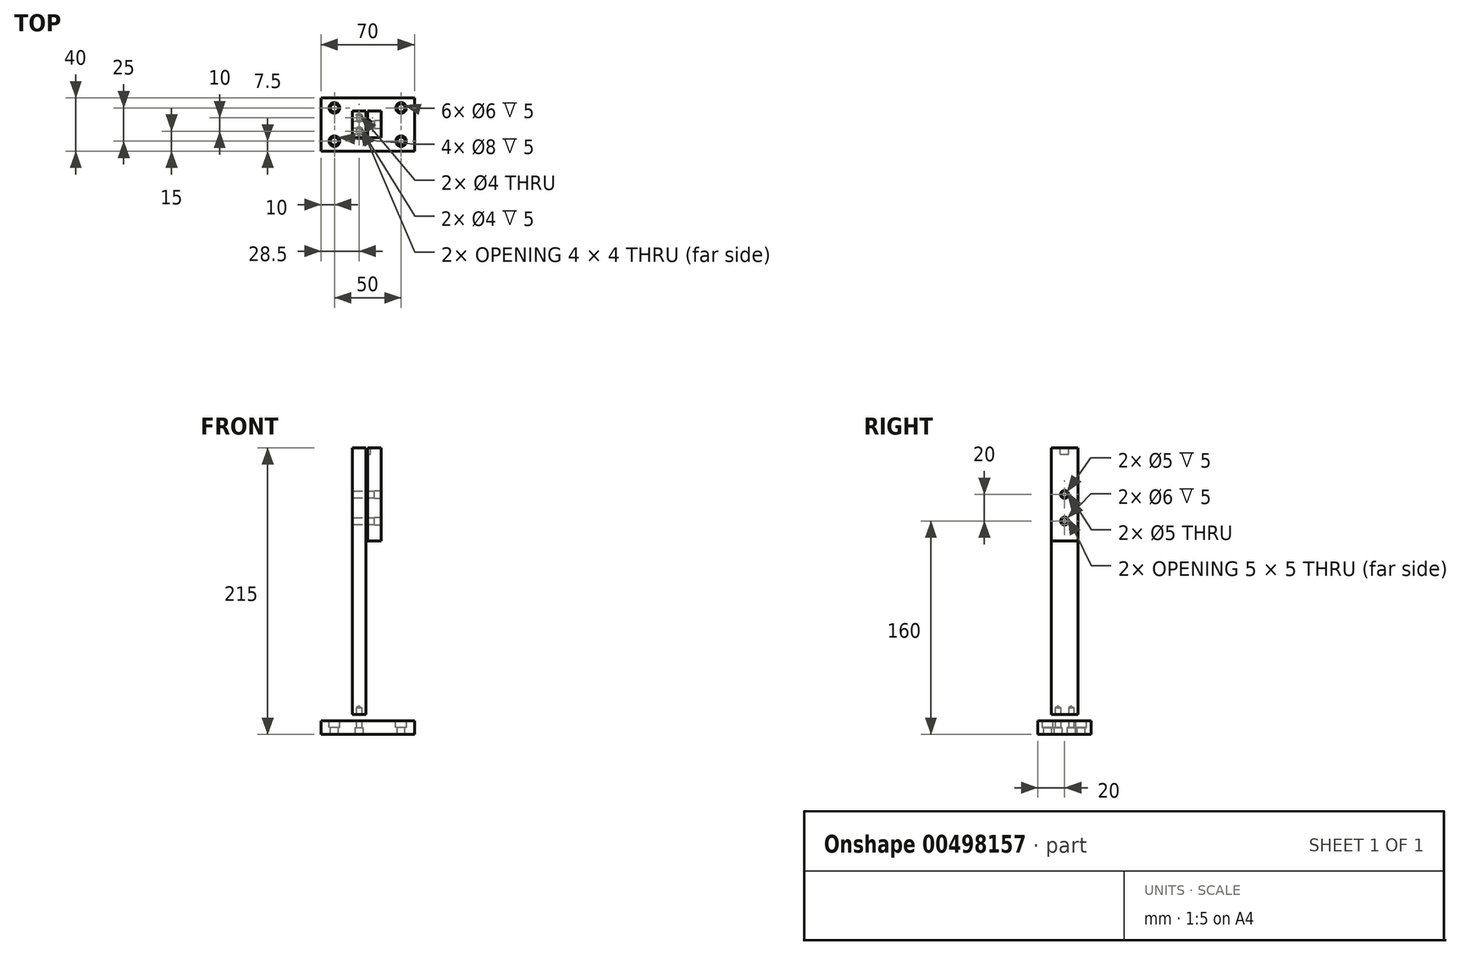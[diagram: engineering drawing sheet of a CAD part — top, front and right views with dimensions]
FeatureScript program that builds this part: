
annotation { "Feature Type Name" : "Feature", "Feature Type Description" : "" }
export const myFeature = defineFeature(function(context is Context, id is Id, definition is map)
    precondition{}
    {
        {
            var Q0;
            Q0=qCreatedBy(makeId("Top.planeOp"),FACE);
            var sketch = newSketch(context, id + "F0", { "sketchPlane" : qUnion([Q0])});
            skLineSegment(sketch, "E0.bottom", {"start": v(-35, 20) * mm, "end": v(35, 20) * mm});
            skLineSegment(sketch, "E0.top", {"start": v(-35, -20) * mm, "end": v(35, -20) * mm});
            skLineSegment(sketch, "E0.left", {"start": v(-35, 20) * mm, "end": v(-35, -20) * mm});
            skLineSegment(sketch, "E0.right", {"start": v(35, 20) * mm, "end": v(35, -20) * mm});
            skPoint(sketch, "E0.middle", {"position": v(0, 0) * mm});
            skSolve(sketch);
        }
        {
            var Q0;
            Q0=makeQuery(id+"F0.imprint","IMPRINT",FACE,{"disambiguationData":[TD([[makeQuery(id+"F0.imprint","IMPRINT",EDGE,{"derivedFrom":sQuery(id+"F0.wireOp",EDGE,"E0.bottom")}),-1.0]])]});
            extrude(context, id + "F1", {"entities" : qUnion([Q0]), "depth" : 10 * mm});
        }
        {
            var Q0;
            Q0=makeQuery(id+"F1.opExtrude","CAP_FACE",FACE,{"disambiguationData":[OSD([sQuery(id+"F0.wireOp",EDGE,"E0.bottom"),sQuery(id+"F0.wireOp",EDGE,"E0.top"),sQuery(id+"F0.wireOp",EDGE,"E0.left"),sQuery(id+"F0.wireOp",EDGE,"E0.right")])],"isStart":false});
            cPlane(context, id + "F2", {"entities" : qUnion([Q0]), "cplaneType" : CPlaneType.OFFSET, "offset" : 0 * mm, "width" : 150 * mm, "height" : 150 * mm});
        }
        {
            var Q0;
            Q0=qCreatedBy(id+"F2.planeOp",FACE);
            var sketch = newSketch(context, id + "F3", { "sketchPlane" : qUnion([Q0])});
            skLineSegment(sketch, "E1.bottom", {"start": v(25, 12.5) * mm, "end": v(-25, 12.5) * mm});
            skLineSegment(sketch, "E1.top", {"start": v(25, -12.5) * mm, "end": v(-25, -12.5) * mm});
            skLineSegment(sketch, "E1.left", {"start": v(25, 12.5) * mm, "end": v(25, -12.5) * mm});
            skLineSegment(sketch, "E1.right", {"start": v(-25, 12.5) * mm, "end": v(-25, -12.5) * mm});
            skPoint(sketch, "E1.middle", {"position": v(0, 0) * mm});
            skSolve(sketch);
        }
        {
            var Q0;
            Q0=sQuery(id+"F3.wireOp",VERTEX,"E1.right.start");
            var Q1;
            Q1=sQuery(id+"F3.wireOp",VERTEX,"E1.bottom.start");
            var Q2;
            Q2=sQuery(id+"F3.wireOp",VERTEX,"E1.left.end");
            var Q3;
            Q3=sQuery(id+"F3.wireOp",VERTEX,"E1.right.end");
            var Q4;
            Q4=makeQuery(id+"F1.opExtrude","SWEPT_BODY",BODY,{"disambiguationData":[OSD([sQuery(id+"F0.wireOp",EDGE,"E0.bottom"),sQuery(id+"F0.wireOp",EDGE,"E0.top"),sQuery(id+"F0.wireOp",EDGE,"E0.left"),sQuery(id+"F0.wireOp",EDGE,"E0.right")])]});
            hole(context, id + "F4", {"style" : HoleStyle.C_BORE, "endStyle" : HoleEndStyle.THROUGH, "holeDiameter" : 6 * mm, "cBoreDiameter" : 8 * mm, "cBoreDepth" : 5 * mm, "isTappedThrough" : true, "tappedDepth" : 12 * mm, "tapClearance" : 3, "startFromSketch" : true, "locations" : qUnion([Q0, Q1, Q2, Q3]), "scope" : qUnion([Q4])});
        }
        {
            var Q0;
            Q0=makeQuery(id+"F1.opExtrude","CAP_FACE",FACE,{"disambiguationData":[OSD([sQuery(id+"F0.wireOp",EDGE,"E0.bottom"),sQuery(id+"F0.wireOp",EDGE,"E0.top"),sQuery(id+"F0.wireOp",EDGE,"E0.left"),sQuery(id+"F0.wireOp",EDGE,"E0.right")])],"isStart":false});
            cPlane(context, id + "F5", {"entities" : qUnion([Q0]), "cplaneType" : CPlaneType.OFFSET, "offset" : 5 * mm, "width" : 150 * mm, "height" : 150 * mm});
        }
        {
            var Q0;
            Q0=qCreatedBy(id+"F5.planeOp",FACE);
            var sketch = newSketch(context, id + "F6", { "sketchPlane" : qUnion([Q0])});
            skLineSegment(sketch, "E2", {"start": v(0, 0) * mm, "end": v(-1.5, 0) * mm});
            skLineSegment(sketch, "E3", {"start": v(-1.5, 0) * mm, "end": v(-11.5, 0) * mm});
            skLineSegment(sketch, "E4", {"start": v(-1.5, 0) * mm, "end": v(-1.5, 10) * mm});
            skLineSegment(sketch, "E5", {"start": v(-1.5, 10) * mm, "end": v(-11.5, 10) * mm});
            skLineSegment(sketch, "E6", {"start": v(-11.5, 10) * mm, "end": v(-11.5, -10) * mm});
            skLineSegment(sketch, "E7", {"start": v(-11.5, -10) * mm, "end": v(-1.5, -10) * mm});
            skLineSegment(sketch, "E8", {"start": v(-1.5, 0) * mm, "end": v(-1.5, -10) * mm});
            skSolve(sketch);
        }
        {
            var Q0;
            {var subQ0=sQuery(id+"F6.wireOp",EDGE,"E3");Q0=makeQuery(id+"F6.imprint","IMPRINT",FACE,{"disambiguationData":[TD([[makeQuery(id+"F6.imprint","IMPRINT",EDGE,{"derivedFrom":subQ0}),-1.0]])]});}
            var Q1;
            {var subQ0=sQuery(id+"F6.wireOp",EDGE,"E3");Q1=makeQuery(id+"F6.imprint","IMPRINT",FACE,{"disambiguationData":[TD([[makeQuery(id+"F6.imprint","IMPRINT",EDGE,{"derivedFrom":subQ0}),1.0]])]});}
            extrude(context, id + "F7", {"entities" : qUnion([Q0, Q1]), "depth" : 200 * mm});
        }
        {
            var Q0;
            Q0=makeQuery(id+"F7.opExtrude","CAP_FACE",FACE,{"disambiguationData":[OSD([sQuery(id+"F6.wireOp",EDGE,"E4"),sQuery(id+"F6.wireOp",EDGE,"E5"),sQuery(id+"F6.wireOp",EDGE,"E6"),sQuery(id+"F6.wireOp",EDGE,"E7"),sQuery(id+"F6.wireOp",EDGE,"E8")])],"isStart":false});
            cPlane(context, id + "F8", {"entities" : qUnion([Q0]), "cplaneType" : CPlaneType.OFFSET, "offset" : 70 * mm, "oppositeDirection" : true, "width" : 150 * mm, "height" : 150 * mm});
        }
        {
            var Q0;
            Q0=qCreatedBy(id+"F8.planeOp",FACE);
            var sketch = newSketch(context, id + "F9", { "sketchPlane" : qUnion([Q0])});
            skLineSegment(sketch, "E9", {"start": v(0, 0) * mm, "end": v(0, 10) * mm});
            skLineSegment(sketch, "E10", {"start": v(0, 10) * mm, "end": v(10, 10) * mm});
            skLineSegment(sketch, "E11", {"start": v(10, 10) * mm, "end": v(10, -10) * mm});
            skLineSegment(sketch, "E12", {"start": v(10, -10) * mm, "end": v(0, -10) * mm});
            skLineSegment(sketch, "E13", {"start": v(0, 0) * mm, "end": v(0, -10) * mm});
            skSolve(sketch);
        }
        {
            var Q0;
            Q0=makeQuery(id+"F9.imprint","IMPRINT",FACE,{"disambiguationData":[TD([[makeQuery(id+"F9.imprint","IMPRINT",EDGE,{"derivedFrom":sQuery(id+"F9.wireOp",EDGE,"E9")}),-1.0]])]});
            extrude(context, id + "F10", {"entities" : qUnion([Q0]), "depth" : 70 * mm});
        }
        {
            var Q0;
            Q0=makeQuery(id+"F10.opExtrude","SWEPT_FACE",FACE,{"disambiguationData":[OSD([sQuery(id+"F9.wireOp",EDGE,"E11")])]});
            cPlane(context, id + "F11", {"entities" : qUnion([Q0]), "cplaneType" : CPlaneType.OFFSET, "offset" : 0 * mm, "width" : 150 * mm, "height" : 150 * mm});
        }
        {
            var Q0;
            Q0=qCreatedBy(id+"F11.planeOp",FACE);
            var sketch = newSketch(context, id + "F12", { "sketchPlane" : qUnion([Q0])});
            skLineSegment(sketch, "E14", {"start": v(0, 0) * mm, "end": v(0, 145) * mm});
            skLineSegment(sketch, "E15", {"start": v(0, 145) * mm, "end": v(0, 160) * mm});
            skLineSegment(sketch, "E16", {"start": v(0, 160) * mm, "end": v(0, 180) * mm});
            skSolve(sketch);
        }
        {
            var Q0;
            Q0=sQuery(id+"F12.wireOp",VERTEX,"E16.start");
            var Q1;
            Q1=sQuery(id+"F12.wireOp",VERTEX,"E16.end");
            var Q2;
            Q2=makeQuery(id+"F7.opExtrude","SWEPT_BODY",BODY,{"disambiguationData":[OSD([sQuery(id+"F6.wireOp",EDGE,"E4"),sQuery(id+"F6.wireOp",EDGE,"E5"),sQuery(id+"F6.wireOp",EDGE,"E6"),sQuery(id+"F6.wireOp",EDGE,"E7"),sQuery(id+"F6.wireOp",EDGE,"E8")])]});
            var Q3;
            Q3=makeQuery(id+"F10.opExtrude","SWEPT_BODY",BODY,{"disambiguationData":[OSD([sQuery(id+"F9.wireOp",EDGE,"E9"),sQuery(id+"F9.wireOp",EDGE,"E10"),sQuery(id+"F9.wireOp",EDGE,"E11"),sQuery(id+"F9.wireOp",EDGE,"E12"),sQuery(id+"F9.wireOp",EDGE,"E13")])]});
            hole(context, id + "F13", {"style" : HoleStyle.C_BORE, "endStyle" : HoleEndStyle.THROUGH, "holeDiameter" : 5 * mm, "cBoreDiameter" : 6 * mm, "cBoreDepth" : 5 * mm, "isTappedThrough" : true, "tappedDepth" : 12 * mm, "tapClearance" : 3, "startFromSketch" : true, "locations" : qUnion([Q0, Q1]), "scope" : qUnion([Q2, Q3])});
        }
        {
            var Q0;
            Q0=qCreatedBy(makeId("Top.planeOp"),FACE);
            var sketch = newSketch(context, id + "F14", { "sketchPlane" : qUnion([Q0])});
            skLineSegment(sketch, "E17", {"start": v(0, 0) * mm, "end": v(-1.5, 0) * mm});
            skLineSegment(sketch, "E18", {"start": v(-1.5, 0) * mm, "end": v(-11.5, 0) * mm});
            skLineSegment(sketch, "E19", {"start": v(-11.5, 0) * mm, "end": v(-11.5, -10) * mm});
            skLineSegment(sketch, "E20", {"start": v(-11.5, -10) * mm, "end": v(-1.5, -10) * mm});
            skLineSegment(sketch, "E21", {"start": v(-1.5, -10) * mm, "end": v(-1.5, 10) * mm});
            skLineSegment(sketch, "E22", {"start": v(-1.5, 10) * mm, "end": v(-11.5, 10) * mm});
            skLineSegment(sketch, "E23", {"start": v(-11.5, 10) * mm, "end": v(-11.5, 0) * mm});
            skLineSegment(sketch, "E24", {"start": v(-11.5, 0) * mm, "end": v(-11.5, -5) * mm});
            skLineSegment(sketch, "E25", {"start": v(-11.5, -5) * mm, "end": v(-1.5, -5) * mm});
            skLineSegment(sketch, "E26", {"start": v(-1.5, -5) * mm, "end": v(-6.5, -5) * mm});
            skLineSegment(sketch, "E27", {"start": v(-11.5, 10) * mm, "end": v(-11.5, 5) * mm});
            skLineSegment(sketch, "E28", {"start": v(-11.5, 5) * mm, "end": v(-6.5, 5) * mm});
            skSolve(sketch);
        }
        {
            var Q0;
            Q0=sQuery(id+"F14.wireOp",VERTEX,"E28.end");
            var Q1;
            Q1=sQuery(id+"F14.wireOp",VERTEX,"E26.end");
            var Q2;
            Q2=makeQuery(id+"F1.opExtrude","SWEPT_BODY",BODY,{"disambiguationData":[OSD([sQuery(id+"F0.wireOp",EDGE,"E0.bottom"),sQuery(id+"F0.wireOp",EDGE,"E0.top"),sQuery(id+"F0.wireOp",EDGE,"E0.left"),sQuery(id+"F0.wireOp",EDGE,"E0.right")])]});
            var Q3;
            Q3=makeQuery(id+"F7.opExtrude","SWEPT_BODY",BODY,{"disambiguationData":[OSD([sQuery(id+"F6.wireOp",EDGE,"E4"),sQuery(id+"F6.wireOp",EDGE,"E5"),sQuery(id+"F6.wireOp",EDGE,"E6"),sQuery(id+"F6.wireOp",EDGE,"E7"),sQuery(id+"F6.wireOp",EDGE,"E8")])]});
            hole(context, id + "F15", {"style" : HoleStyle.C_BORE, "endStyle" : HoleEndStyle.BLIND, "oppositeDirection" : true, "holeDiameter" : 4 * mm, "cBoreDiameter" : 6 * mm, "cBoreDepth" : 5 * mm, "holeDepth" : 20 * mm, "isTappedThrough" : true, "tappedDepth" : 12 * mm, "tapClearance" : 3, "startFromSketch" : true, "locations" : qUnion([Q0, Q1]), "scope" : qUnion([Q2, Q3])});
        }
        {
            var Q0;
            Q0=makeQuery(id+"F10.opExtrude","CAP_FACE",FACE,{"disambiguationData":[OSD([sQuery(id+"F9.wireOp",EDGE,"E9"),sQuery(id+"F9.wireOp",EDGE,"E10"),sQuery(id+"F9.wireOp",EDGE,"E11"),sQuery(id+"F9.wireOp",EDGE,"E12"),sQuery(id+"F9.wireOp",EDGE,"E13")])],"isStart":false});
            cPlane(context, id + "F16", {"entities" : qUnion([Q0]), "cplaneType" : CPlaneType.OFFSET, "offset" : 0 * mm, "width" : 150 * mm, "height" : 150 * mm});
        }
        {
            var Q0;
            Q0=qCreatedBy(id+"F16.planeOp",FACE);
            var sketch = newSketch(context, id + "F17", { "sketchPlane" : qUnion([Q0])});
            skLineSegment(sketch, "E29", {"start": v(0, 0) * mm, "end": v(2, 0) * mm});
            skLineSegment(sketch, "E30", {"start": v(0, 0) * mm, "end": v(0, 3.17) * mm});
            skLineSegment(sketch, "E31", {"start": v(0, 0) * mm, "end": v(0, -3.17) * mm});
            skLineSegment(sketch, "E32", {"start": v(0, -3.17) * mm, "end": v(2, -3.17) * mm});
            skLineSegment(sketch, "E33", {"start": v(0, 3.17) * mm, "end": v(2, 3.17) * mm});
            skLineSegment(sketch, "E34", {"start": v(2, 3.17) * mm, "end": v(2, -3.17) * mm});
            skSolve(sketch);
        }
        {
            var Q0;
            {var subQ0=sQuery(id+"F17.wireOp",EDGE,"E29");Q0=makeQuery(id+"F17.imprint","IMPRINT",FACE,{"disambiguationData":[TD([[makeQuery(id+"F17.imprint","IMPRINT",EDGE,{"derivedFrom":subQ0}),1.0]])]});}
            var Q1;
            {var subQ0=sQuery(id+"F17.wireOp",EDGE,"E29");Q1=makeQuery(id+"F17.imprint","IMPRINT",FACE,{"disambiguationData":[TD([[makeQuery(id+"F17.imprint","IMPRINT",EDGE,{"derivedFrom":subQ0}),-1.0]])]});}
            extrude(context, id + "F18", {"entities" : qUnion([Q0, Q1]), "operationType" : NewBodyOperationType.REMOVE, "oppositeDirection" : true, "depth" : 5 * mm});
        }
        {
            var Q0;
            Q0=makeQuery(id+"F7.opExtrude","SWEPT_FACE",FACE,{"disambiguationData":[OSD([sQuery(id+"F6.wireOp",EDGE,"E7")])]});
            cPlane(context, id + "F19", {"entities" : qUnion([Q0]), "cplaneType" : CPlaneType.OFFSET, "offset" : 0 * mm, "width" : 150 * mm, "height" : 150 * mm});
        }
        {
            var Q0;
            Q0=makeQuery(id+"F10.opExtrude","SWEPT_FACE",FACE,{"disambiguationData":[OSD([sQuery(id+"F9.wireOp",EDGE,"E11")])]});
            cPlane(context, id + "F20", {"entities" : qUnion([Q0]), "cplaneType" : CPlaneType.OFFSET, "offset" : 0 * mm, "width" : 150 * mm, "height" : 150 * mm});
        }
    });
